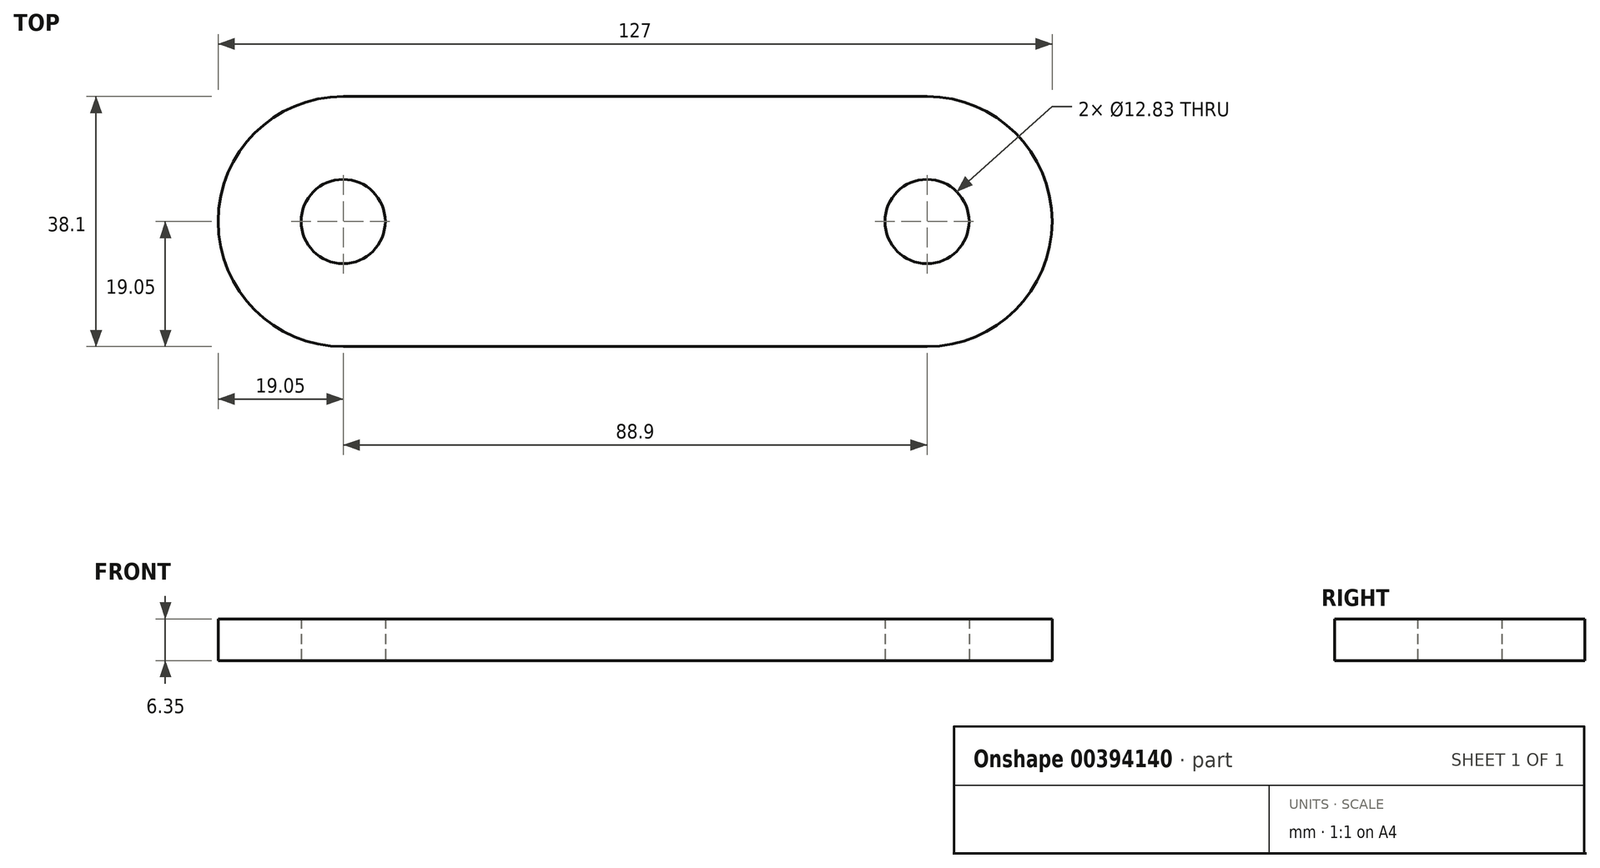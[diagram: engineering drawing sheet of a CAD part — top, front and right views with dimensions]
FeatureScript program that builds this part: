
annotation { "Feature Type Name" : "Feature", "Feature Type Description" : "" }
export const myFeature = defineFeature(function(context is Context, id is Id, definition is map)
    precondition{}
    {
        {
            var Q0;
            Q0=qCreatedBy(makeId("Top.planeOp"),FACE);
            var sketch = newSketch(context, id + "F0", { "sketchPlane" : qUnion([Q0])});
            skLineSegment(sketch, "E0.bottom", {"start": v(-44.45, 19.05) * mm, "end": v(44.45, 19.05) * mm});
            skLineSegment(sketch, "E0.top", {"start": v(-44.45, -19.05) * mm, "end": v(44.45, -19.05) * mm});
            skArc(sketch, "E1", {"start": v(-44.45, 19.05) * mm, "mid": v(-63.5, 0) * mm, "end": v(-44.45, -19.05) * mm});
            skArc(sketch, "E2.MirrorC", {"start": v(44.45, 19.05) * mm, "mid": v(63.5, 0) * mm, "end": v(44.45, -19.05) * mm});
            skCircle(sketch, "E3", {"center": v(-44.45, 0) * mm, "radius": 6.41 * mm});
            skCircle(sketch, "E4.MirrorC", {"center": v(44.45, 0) * mm, "radius": 6.41 * mm});
            skSolve(sketch);
        }
        {
            var Q0;
            Q0=makeQuery(id+"F0.imprint","IMPRINT",FACE,{"disambiguationData":[TD([[makeQuery(id+"F0.imprint","IMPRINT",EDGE,{"derivedFrom":sQuery(id+"F0.wireOp",EDGE,"E0.bottom")}),-1.0]])]});
            extrude(context, id + "F1", {"entities" : qUnion([Q0]), "depth" : 6.35 * mm});
        }
    });
